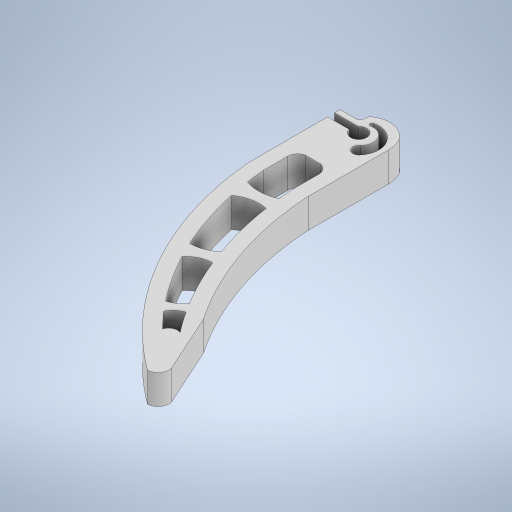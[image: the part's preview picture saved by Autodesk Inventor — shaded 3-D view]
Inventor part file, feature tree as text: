
AUTODESK INVENTOR PART (.ipt)
format: ipt  version: 2024 (Build 280153000, 153)  size: 836,096 bytes
history: native  units: in
note: dims shown in document units (in); Inventor stores cm internally (conversion verified against a paired STEP export)
features: sketch x8, extrude x5, fillet x3, hole x2, projected_geometry x1
ambient origin geometry x8: Origin, YZ Plane, XZ Plane, XY Plane, X Axis, Y Axis, Z Axis, Center Point
bodies: Solid1 (feature_tree)
feature tree (19):
  extrude  "Extrusion1"  Depth=0.175in
  fillet  "Fillet1"  Radius=2.0in
  hole  "Hole1"  [1 undecoded]
  hole  "Hole2"  [1 undecoded]
  extrude  "Extrusion2"  Depth=0.25in
  extrude  "Extrusion4"  Depth=0.75in
  fillet  "Fillet2"  Radius=1.1671in
  fillet  "Fillet3"  Radius=0.75in
  extrude  "FOR EXTERIOR"  Depth=0.36in
  extrude  "For Exterior claw"  Depth=0.05in
  sketch  "Sketch9"  dims[d44=0.2in d45=0.375in d46=0.21in d47=0.75in d48=0.375in d49=0.25in d50=0.5635in d51=1.0in d52=0.0in d53=0.22in d54=0.75in d55=0.375in d56=0.25in d57=0.5635in d58=0.4in d59=0.0in d63=0.2in d65=0.26in d66=0.26in d67=0.7in d68=0.45in d69=0.0in d90=0.12in d91=0.1in d92=1.0in d93=0.0in d94=0.125in d95=0.125in d96=0.403in d97=1.0in d98=0.0in d99=1.0in d100=0.0in]
  sketch  "Sketch1"  dims[d17=0.318in d19=0.175in d22=2.0in]
  sketch  "Sketch2"  dims[d26=0.36in d27=0.35in]
  sketch  "Sketch3"  dims[d28=0.35in d29=0.36in]
  sketch  "Sketch4"  dims[d31=180.0deg d32=0.25in]
  projected_geometry  "Projected Loop1"
  sketch  "Sketch6"  dims[d33=8.1548in d34=1.3328in d35=1.1671in d36=0.75in]
  sketch  "Sketch7"  dims[d37=0.1334in d39=0.36in]
  sketch  "Sketch8"  dims[d40=0.75in d41=0.0in d43=0.05in]
note: 2 required parameter values undecoded (feature->parameter linkage not recoverable at this tier; creation-order binding heuristic only, values carry confidence <= 0.55)
